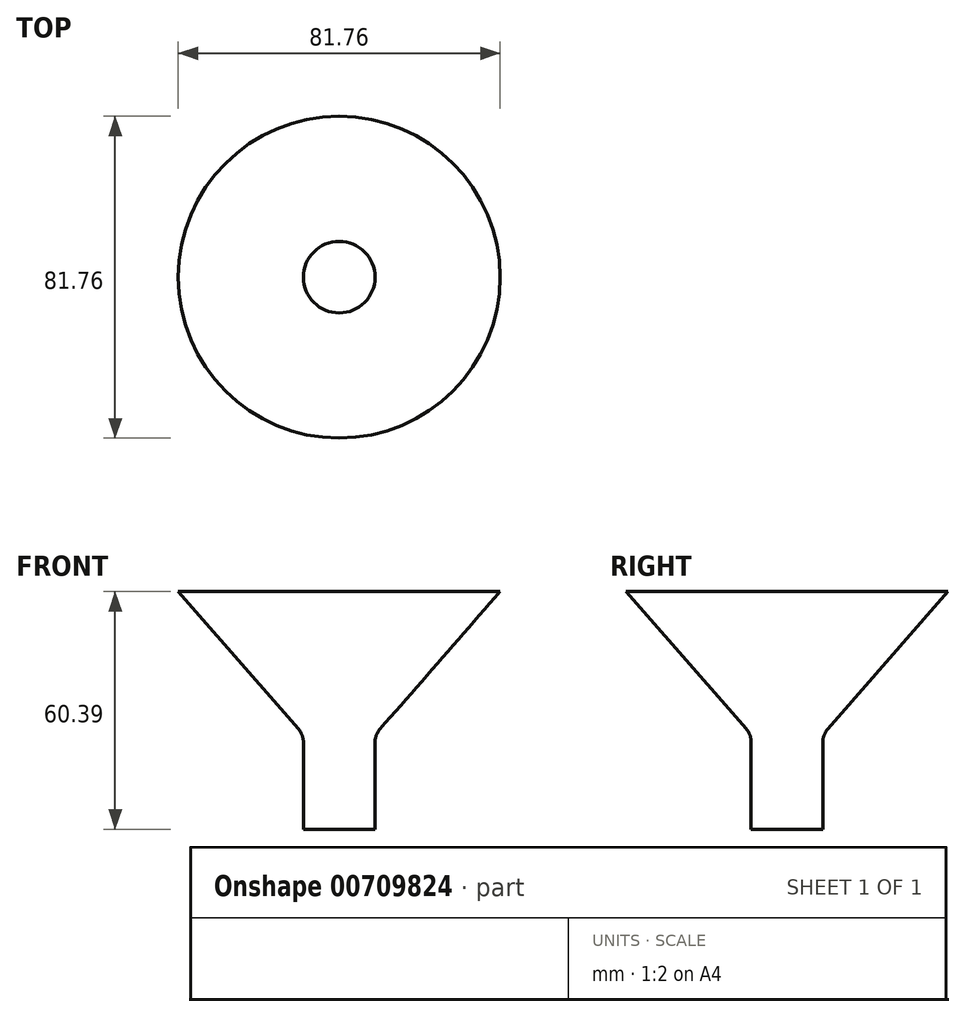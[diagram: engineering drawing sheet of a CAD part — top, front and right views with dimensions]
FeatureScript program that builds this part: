
annotation { "Feature Type Name" : "Feature", "Feature Type Description" : "" }
export const myFeature = defineFeature(function(context is Context, id is Id, definition is map)
    precondition{}
    {
        {
            var Q0;
            Q0=qCreatedBy(makeId("Front.planeOp"),FACE);
            var sketch = newSketch(context, id + "F0", { "sketchPlane" : qUnion([Q0])});
            skLineSegment(sketch, "E0", {"start": v(0, 0) * mm, "end": v(-9.1, 0) * mm});
            skLineSegment(sketch, "E1", {"start": v(-9.1, 0) * mm, "end": v(-9.1, 24) * mm});
            skLineSegment(sketch, "E2", {"start": v(-9.1, 24) * mm, "end": v(-40.88, 60.4) * mm});
            skLineSegment(sketch, "E3", {"start": v(-40.88, 60.4) * mm, "end": v(0, 60.4) * mm});
            skLineSegment(sketch, "E4", {"start": v(0, 60.4) * mm, "end": v(0, 0) * mm});
            skSolve(sketch);
        }
        {
            var Q0;
            Q0=sQuery(id+"F0.wireOp",EDGE,"E2");
            var Q1;
            Q1=sQuery(id+"F0.wireOp",EDGE,"E1");
            var Q2;
            Q2=sQuery(id+"F0.wireOp",EDGE,"E4");
            revolve(context, id + "F1", {"bodyType" : ToolBodyType.SURFACE, "surfaceOperationType" : NewSurfaceOperationType.NEW, "surfaceEntities" : qUnion([Q0, Q1]), "axis" : qUnion([Q2]), "revolveType" : RevolveType.FULL});
        }
        {
            var Q0;
            Q0=makeQuery(id+"F1.opRevolve","SWEPT_FACE",FACE,{"disambiguationData":[OSD([sQuery(id+"F0.wireOp",EDGE,"E2")])]});
            var Q1;
            Q1=makeQuery(id+"F1.opRevolve","SWEPT_FACE",FACE,{"disambiguationData":[OSD([sQuery(id+"F0.wireOp",EDGE,"E1")])]});
            fillet(context, id + "F2", {"entities" : qUnion([Q0, Q1]), "radius" : 5.08 * mm, "tangentPropagation" : true, "allowEdgeOverflow" : false});
        }
    });
